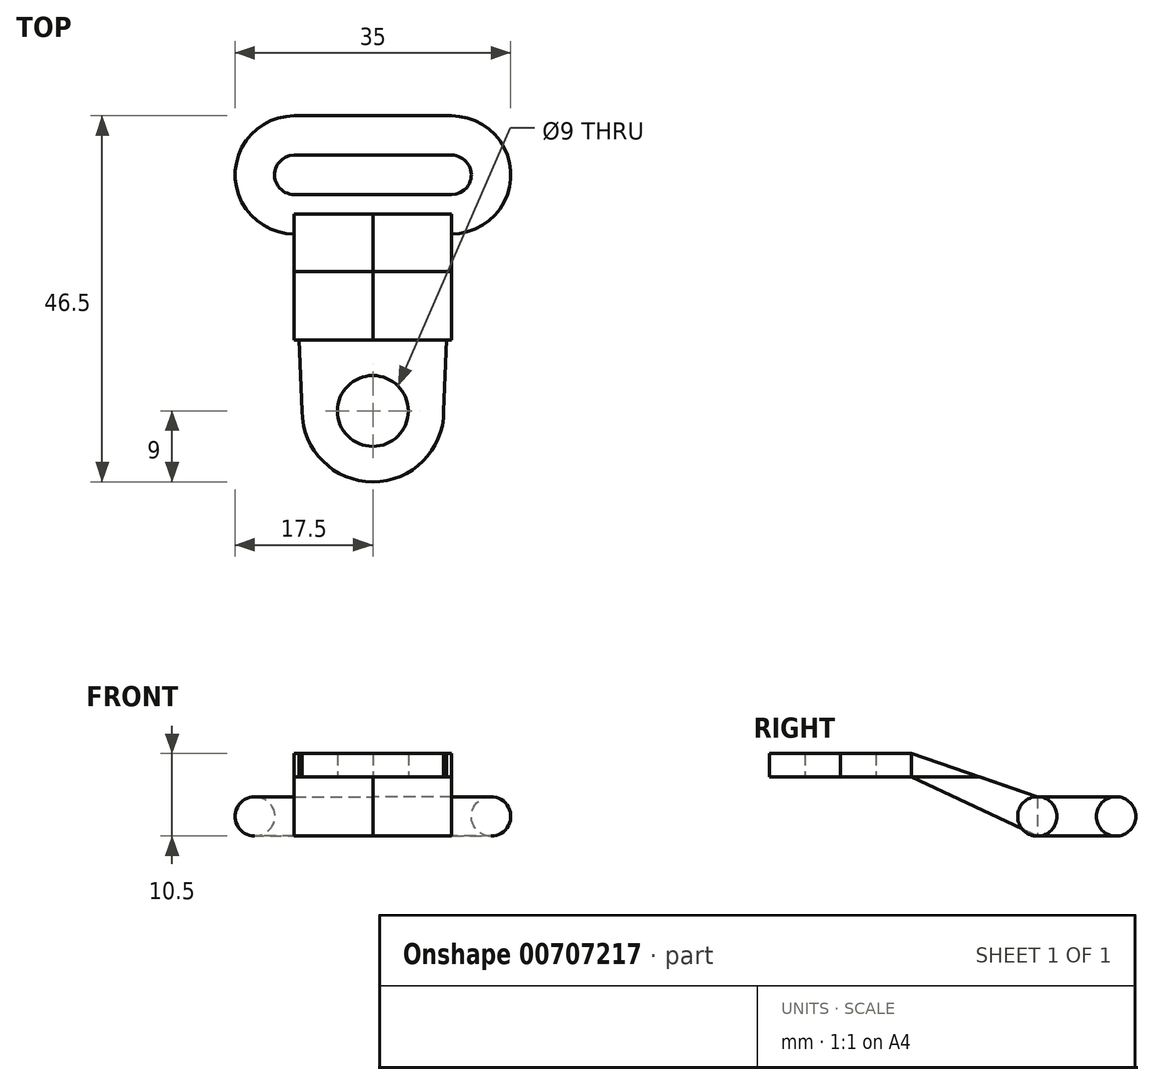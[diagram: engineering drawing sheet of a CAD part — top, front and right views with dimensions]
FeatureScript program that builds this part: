
annotation { "Feature Type Name" : "Feature", "Feature Type Description" : "" }
export const myFeature = defineFeature(function(context is Context, id is Id, definition is map)
    precondition{}
    {
        {
            var Q0;
            Q0=qCreatedBy(makeId("Top.planeOp"),FACE);
            var sketch = newSketch(context, id + "F0", { "sketchPlane" : qUnion([Q0])});
            skLineSegment(sketch, "E0.bottom", {"start": v(-10, 2.5) * mm, "end": v(10, 2.5) * mm});
            skLineSegment(sketch, "E0.top", {"start": v(-10, -2.5) * mm, "end": v(10, -2.5) * mm});
            skPoint(sketch, "E0.middle", {"position": v(0, 0) * mm});
            skLineSegment(sketch, "E1", {"start": v(-10, -7.5) * mm, "end": v(10, -7.5) * mm});
            skLineSegment(sketch, "E2", {"start": v(-10, 7.5) * mm, "end": v(10, 7.5) * mm});
            skArc(sketch, "E3", {"start": v(-10, 7.5) * mm, "mid": v(-17.5, 0) * mm, "end": v(-10, -7.5) * mm});
            skArc(sketch, "E4", {"start": v(10, 7.5) * mm, "mid": v(17.5, 0) * mm, "end": v(10, -7.5) * mm});
            skArc(sketch, "E5", {"start": v(10, -2.5) * mm, "mid": v(12.5, 0) * mm, "end": v(10, 2.5) * mm});
            skArc(sketch, "E6", {"start": v(-10, -2.5) * mm, "mid": v(-12.5, 0) * mm, "end": v(-10, 2.5) * mm});
            skSolve(sketch);
        }
        {
            var Q0;
            Q0=qCreatedBy(makeId("Right.planeOp"),FACE);
            var sketch = newSketch(context, id + "F1", { "sketchPlane" : qUnion([Q0])});
            skPoint(sketch, "E7", {"position": v(-5, 0) * mm});
            skCircle(sketch, "E8", {"center": v(-5, 0) * mm, "radius": 2.5 * mm});
            skSolve(sketch);
        }
        {
            var Q0;
            Q0=qCreatedBy(makeId("Top.planeOp"),FACE);
            cPlane(context, id + "F2", {"entities" : qUnion([Q0]), "cplaneType" : CPlaneType.OFFSET, "offset" : 5 * mm, "width" : 150 * mm, "height" : 150 * mm});
        }
        {
            var Q0;
            Q0=qCreatedBy(id+"F2.planeOp",FACE);
            var sketch = newSketch(context, id + "F3", { "sketchPlane" : qUnion([Q0])});
            skPoint(sketch, "E9", {"position": v(0, -30) * mm});
            skCircle(sketch, "E10", {"center": v(0, -30) * mm, "radius": 4.5 * mm});
            skCircle(sketch, "E11", {"center": v(0, -30) * mm, "radius": 9 * mm});
            skSolve(sketch);
        }
        {
            var Q0;
            Q0 = qSketchRegion(id + "F3", true);
            extrude(context, id + "F4", {"entities" : qUnion([Q0]), "depth" : 3 * mm, "offsetDistance" : 25 * mm});
        }
        {
            var Q0;
            Q0=qCreatedBy(id+"F2.planeOp",FACE);
            var sketch = newSketch(context, id + "F5", { "sketchPlane" : qUnion([Q0])});
            skPoint(sketch, "E12", {"position": v(-37.08, -21.1) * mm});
            skPoint(sketch, "E13", {"position": v(-25.48, -25.42) * mm});
            skPoint(sketch, "E14", {"position": v(0, -30) * mm});
            skPoint(sketch, "E15", {"position": v(17.5, 0) * mm});
            skPoint(sketch, "E16", {"position": v(-17.5, 0) * mm});
            skPoint(sketch, "E17", {"position": v(0, -5) * mm});
            skPoint(sketch, "E18", {"position": v(-10, -5) * mm});
            skPoint(sketch, "E19", {"position": v(10, -5) * mm});
            skLineSegment(sketch, "E20", {"start": v(-10, -5) * mm, "end": v(10, -5) * mm});
            skPoint(sketch, "E21", {"position": v(-9, -30) * mm});
            skPoint(sketch, "E22", {"position": v(9, -30) * mm});
            skLineSegment(sketch, "E23", {"start": v(-9, -30) * mm, "end": v(-10, -5) * mm});
            skLineSegment(sketch, "E24", {"start": v(10, -5) * mm, "end": v(9, -30) * mm});
            skLineSegment(sketch, "E25", {"start": v(-9, -30) * mm, "end": v(-1.42, -23.65) * mm});
            skLineSegment(sketch, "E26", {"start": v(-1.42, -23.65) * mm, "end": v(9, -30) * mm});
            skSolve(sketch);
        }
        {
            var Q0;
            Q0 = qSketchRegion(id + "F5", true);
            extrude(context, id + "F6", {"entities" : qUnion([Q0]), "operationType" : NewBodyOperationType.ADD, "depth" : 3 * mm, "offsetDistance" : 25 * mm});
        }
        {
            var Q0;
            Q0=qCreatedBy(id+"F2.planeOp",FACE);
            var sketch = newSketch(context, id + "F7", { "sketchPlane" : qUnion([Q0])});
            skPoint(sketch, "E27", {"position": v(0, -30) * mm});
            skPoint(sketch, "E28", {"position": v(-17.34, -24.35) * mm});
            skPoint(sketch, "E29", {"position": v(0, -21) * mm});
            skLineSegment(sketch, "E30", {"start": v(0, -21) * mm, "end": v(-13.31, -21) * mm});
            skLineSegment(sketch, "E31", {"start": v(-13.31, -21) * mm, "end": v(13.6, -21) * mm});
            skLineSegment(sketch, "E32", {"start": v(13.6, -21) * mm, "end": v(13.6, -1.76) * mm});
            skLineSegment(sketch, "E33", {"start": v(13.6, -1.76) * mm, "end": v(-14.46, -1.76) * mm});
            skLineSegment(sketch, "E34", {"start": v(-14.46, -1.76) * mm, "end": v(-13.31, -21) * mm});
            skSolve(sketch);
        }
        {
            var Q0;
            Q0 = qSketchRegion(id + "F7", true);
            extrude(context, id + "F8", {"entities" : qUnion([Q0]), "operationType" : NewBodyOperationType.REMOVE, "depth" : 3.1 * mm, "offsetDistance" : 25 * mm});
        }
        {
            var Q0;
            Q0=qCreatedBy(makeId("Right.planeOp"),FACE);
            var sketch = newSketch(context, id + "F9", { "sketchPlane" : qUnion([Q0])});
            skPoint(sketch, "E35", {"position": v(-5, 0) * mm});
            skPoint(sketch, "E36", {"position": v(-5, 2.5) * mm});
            skPoint(sketch, "E37", {"position": v(-5, -2.5) * mm});
            skPoint(sketch, "E38", {"position": v(-21, 5) * mm});
            skPoint(sketch, "E39", {"position": v(-21, 8) * mm});
            skLineSegment(sketch, "E40", {"start": v(-5, -2.5) * mm, "end": v(-21, 5) * mm});
            skLineSegment(sketch, "E41", {"start": v(-21, 8) * mm, "end": v(-5, 2.5) * mm});
            skLineSegment(sketch, "E42", {"start": v(-21, 8) * mm, "end": v(-21, 5) * mm});
            skLineSegment(sketch, "E43", {"start": v(-5, 2.5) * mm, "end": v(-5, -2.5) * mm});
            skSolve(sketch);
        }
        {
            var Q0;
            Q0 = qSketchRegion(id + "F9", true);
            extrude(context, id + "F10", {"entities" : qUnion([Q0]), "depth" : 10 * mm, "offsetDistance" : 25 * mm});
        }
        {
            var Q0;
            Q0 = qSketchRegion(id + "F9", true);
            extrude(context, id + "F11", {"entities" : qUnion([Q0]), "oppositeDirection" : true, "depth" : 10 * mm, "offsetDistance" : 25 * mm});
        }
        {
            var Q0;
            Q0=makeQuery(id+"F1.imprint","IMPRINT",FACE,{"disambiguationData":[TD([[makeQuery(id+"F1.imprint","IMPRINT",EDGE,{"derivedFrom":sQuery(id+"F1.wireOp",EDGE,"E8")}),1.0]])]});
            var Q1;
            Q1=sQuery(id+"F0.wireOp",EDGE,"E0.top");
            var Q2;
            Q2=sQuery(id+"F0.wireOp",EDGE,"E6");
            var Q3;
            Q3=sQuery(id+"F0.wireOp",EDGE,"E0.bottom");
            var Q4;
            Q4=sQuery(id+"F0.wireOp",EDGE,"E5");
            sweep(context, id + "F12", {"profiles" : qUnion([Q0]), "path" : qUnion([Q1, Q2, Q3, Q4])});
        }
    });
